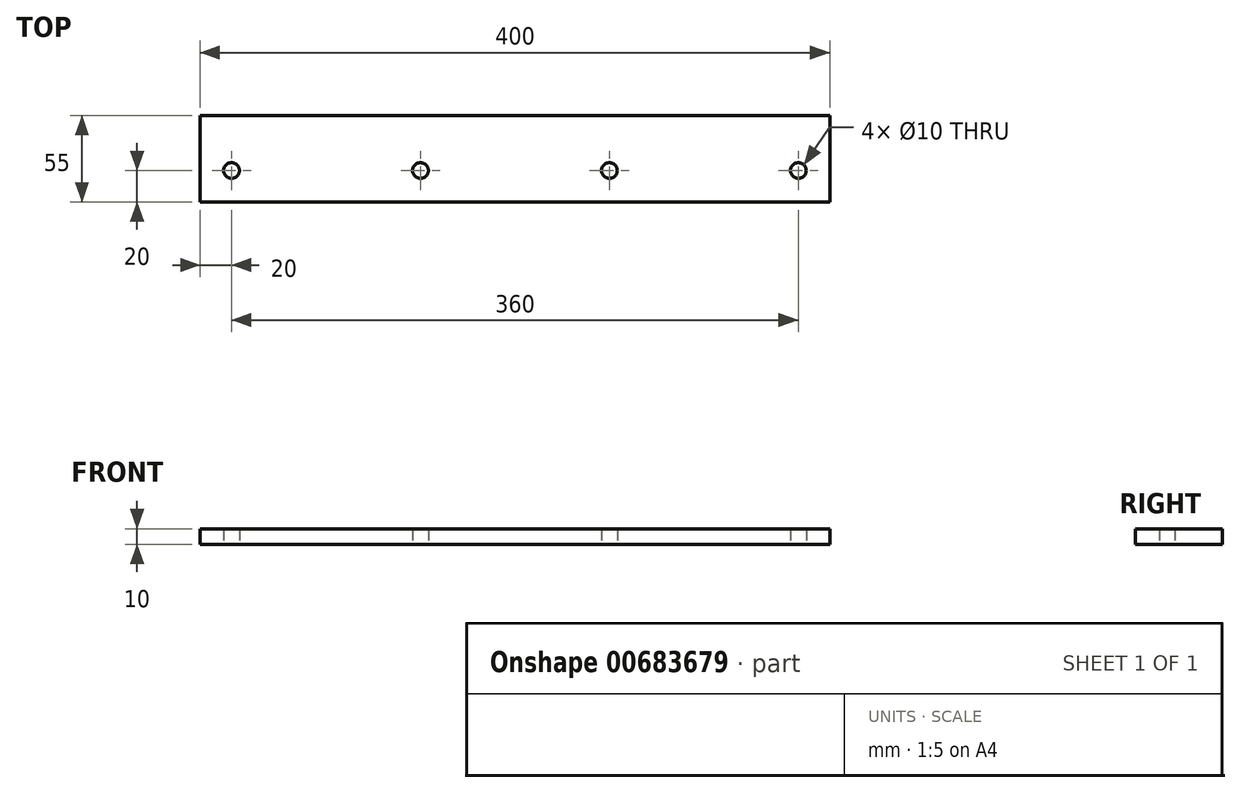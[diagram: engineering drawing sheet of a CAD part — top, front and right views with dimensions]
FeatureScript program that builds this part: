
annotation { "Feature Type Name" : "Feature", "Feature Type Description" : "" }
export const myFeature = defineFeature(function(context is Context, id is Id, definition is map)
    precondition{}
    {
        {
            var Q0;
            Q0=qCreatedBy(makeId("Top.planeOp"),FACE);
            var sketch = newSketch(context, id + "F0", { "sketchPlane" : qUnion([Q0])});
            skLineSegment(sketch, "E0.bottom", {"start": v(0, 0) * mm, "end": v(400, 0) * mm});
            skLineSegment(sketch, "E0.top", {"start": v(0, 55) * mm, "end": v(400, 55) * mm});
            skLineSegment(sketch, "E0.left", {"start": v(0, 0) * mm, "end": v(0, 55) * mm});
            skLineSegment(sketch, "E0.right", {"start": v(400, 0) * mm, "end": v(400, 55) * mm});
            skCircle(sketch, "E1", {"center": v(20, 20) * mm, "radius": 5 * mm});
            skCircle(sketch, "E2.1.0.0", {"center": v(140, 20) * mm, "radius": 5 * mm});
            skCircle(sketch, "E2.2.0.0", {"center": v(260, 20) * mm, "radius": 5 * mm});
            skCircle(sketch, "E2.3.0.0", {"center": v(380, 20) * mm, "radius": 5 * mm});
            skLineSegment(sketch, "E2.direction1", {"start": v(20, 20) * mm, "end": v(140, 20) * mm, "construction": true});
            skSolve(sketch);
        }
        {
            var Q0;
            Q0=makeQuery(id+"F0.imprint","IMPRINT",FACE,{"disambiguationData":[TD([[makeQuery(id+"F0.imprint","IMPRINT",EDGE,{"derivedFrom":sQuery(id+"F0.wireOp",EDGE,"E0.bottom")}),1.0]])]});
            extrude(context, id + "F1", {"entities" : qUnion([Q0]), "depth" : 10 * mm, "offsetDistance" : 25 * mm});
        }
    });
